# Revit family: Gira_503405
name_source: partatom
category: Elektroinstallationen
revit_build: Autodesk Revit 2017 (Build: 20160225_1515(x64)
units: mm (PartAtom-declared; Revit-internal decimal feet)

## family parameters
Basisbauteil = Fläche
Beim Laden mit Abzugskörper schneiden = Nein
Bemaßung runder Anschluss = Durchmesser verwenden
Beschriftungsausrichtung beibehalten = Nein
Gemeinsam genutzt = Nein
Raumberechnungspunkt = Nein
Teiletyp = Normal

## types (1)
- Wippenset 4f indiv. Tastsens.4 TS4 G Schwarz
    Andere Bussysteme = ohne
    BIM = https://media.stage.bim.site TS4 Wippenset 4fach.rfa
    BIMSITE_PRODUCT_ID = 93ec3f111b7558bc4b2acb086ce6e62b1225653b
    Beschreibung = Wippenset 4fach individuell für Tastsensor 4  Glas Schwarz Hinweise :  Beschreibbare Wippensets können mit einer individuellen Beschriftung versehen werden. Die Bestellung wird über den Großhandel abgewickelt, der beim Bestellvorgang der Wippen angegeben wurde.  Dieses Produkt kann ausschließlich über den Gira Beschriftungsservice bestellt werden.  Professionelle Beschriftung über den Gira Beschriftungsservice www.beschriftung.gira.de.
    Bussystem Funkbus = Nein
    Bussystem KNX = Ja
    Bussystem KNX-Funk = Nein
    Bussystem LON = Nein
    Bussystem Powernet = Nein
    Datenblatt = https://media.stage.bim.site
    Datenblatt 1 = https://media.stage.bim.site
    Farbe = schwarz
    Funk bidirektional = Nein
    GTIN = 4010337072522
    HAN = 503405
    HeinzeBIM = https://www.heinze.de
    Hersteller = Gira
    Kosten = 0 $
    Produktseite = https://media.stage.bim.site
    Transparent = Nein
    Typname = Wippenset 4f indiv. Tastsens.4 TS4 G Schwarz
    URL = https://www.gira.de
    Vorgabe-Ansicht = 1219 mm
    Werkstoff Text = Glas

## geometry (parser evidence)
native form markers: Sweep x5
no freeform markers — native parametric forms only
